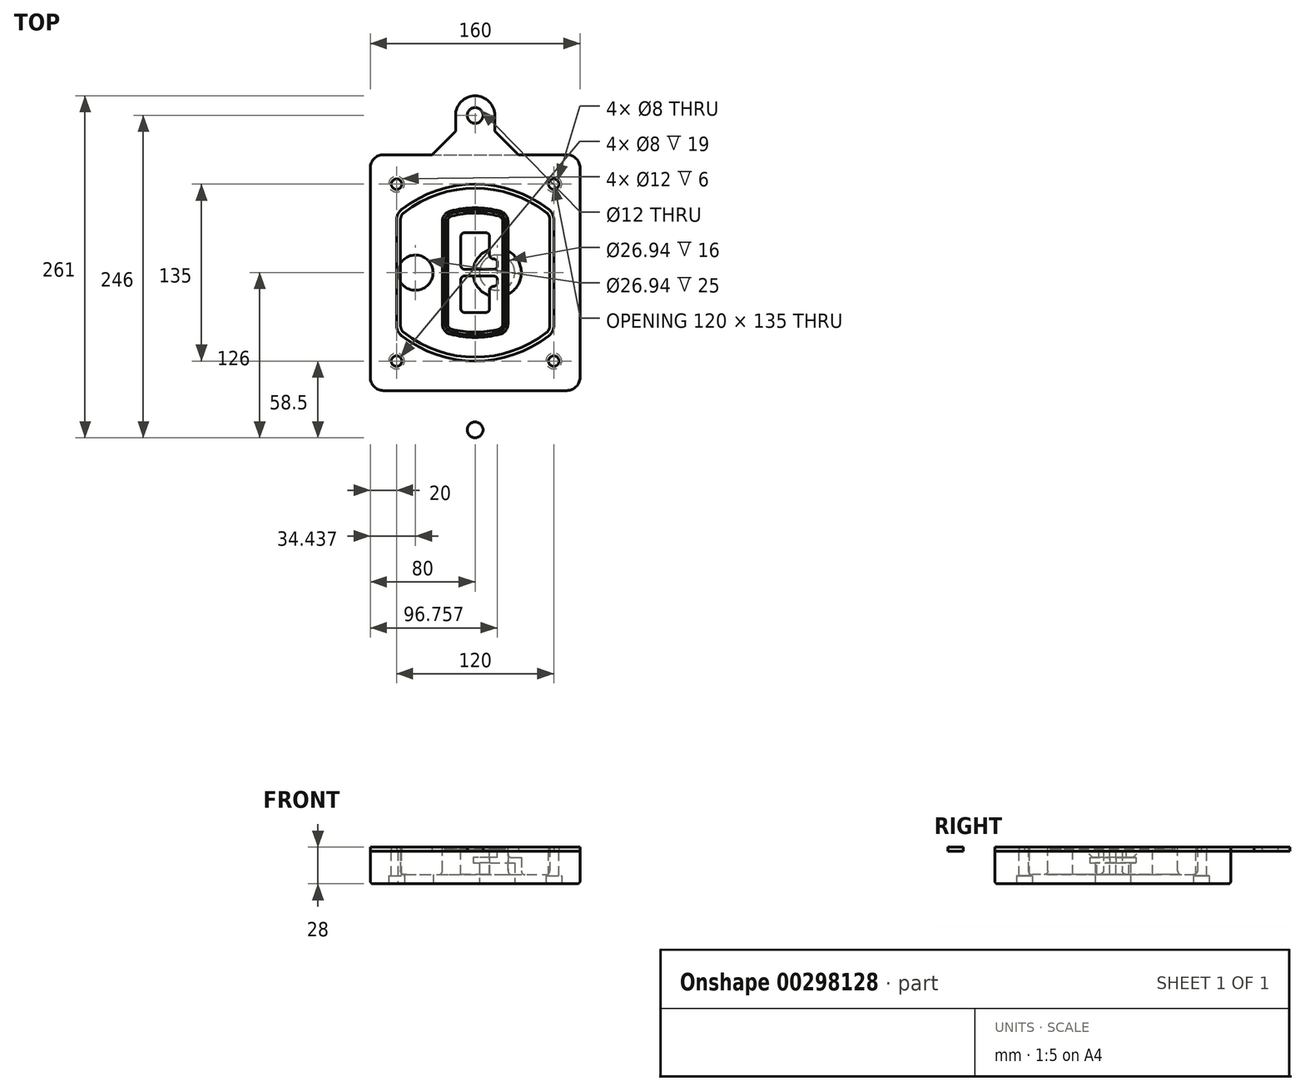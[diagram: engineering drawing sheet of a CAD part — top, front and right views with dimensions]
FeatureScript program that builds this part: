
annotation { "Feature Type Name" : "Feature", "Feature Type Description" : "" }
export const myFeature = defineFeature(function(context is Context, id is Id, definition is map)
    precondition{}
    {
        {
            var Q0;
            Q0=qCreatedBy(makeId("Top.planeOp"),FACE);
            var sketch = newSketch(context, id + "F0", { "sketchPlane" : qUnion([Q0])});
            skPoint(sketch, "E0.rect.middle", {"position": v(0, 0) * mm});
            skLineSegment(sketch, "E1.bottom", {"start": v(-70, -90) * mm, "end": v(70, -90) * mm});
            skLineSegment(sketch, "E1.top", {"start": v(-70, 90) * mm, "end": v(70, 90) * mm});
            skLineSegment(sketch, "E1.left", {"start": v(-80, -80) * mm, "end": v(-80, 80) * mm});
            skLineSegment(sketch, "E1.right", {"start": v(80, -80) * mm, "end": v(80, 80) * mm});
            skLineSegment(sketch, "E2", {"start": v(-80, 90) * mm, "end": v(80, -90) * mm, "construction": true});
            skLineSegment(sketch, "E3", {"start": v(80, 90) * mm, "end": v(-80, -90) * mm, "construction": true});
            skCircle(sketch, "E4", {"center": v(-60, 67.5) * mm, "radius": 4 * mm});
            skCircle(sketch, "E5", {"center": v(60, 67.5) * mm, "radius": 4 * mm});
            skCircle(sketch, "E6", {"center": v(60, -67.5) * mm, "radius": 4 * mm});
            skCircle(sketch, "E7", {"center": v(-60, -67.5) * mm, "radius": 4 * mm});
            skLineSegment(sketch, "E8", {"start": v(-60, 67.5) * mm, "end": v(60, 67.5) * mm, "construction": true});
            skLineSegment(sketch, "E9", {"start": v(60, 67.5) * mm, "end": v(60, -67.5) * mm, "construction": true});
            skLineSegment(sketch, "E10", {"start": v(60, -67.5) * mm, "end": v(-60, -67.5) * mm, "construction": true});
            skLineSegment(sketch, "E11", {"start": v(-60, -67.5) * mm, "end": v(-60, 67.5) * mm, "construction": true});
            skLineSegment(sketch, "E12", {"start": v(-60, 40.3) * mm, "end": v(-60, -40.3) * mm});
            skLineSegment(sketch, "E13", {"start": v(60, 40.3) * mm, "end": v(60, -40.3) * mm});
            skArc(sketch, "E14", {"start": v(56.15, 48.18) * mm, "mid": v(0, 67.5) * mm, "end": v(-56.15, 48.18) * mm});
            skArc(sketch, "E15", {"start": v(-56.15, -48.18) * mm, "mid": v(0, -67.5) * mm, "end": v(56.15, -48.18) * mm});
            skLineSegment(sketch, "E16", {"start": v(-60, 0) * mm, "end": v(60, 0) * mm, "construction": true});
            skPoint(sketch, "E17.visualSharp", {"position": v(-60, -45) * mm});
            skArc(sketch, "E17.filletArc", {"start": v(-60, -40.3) * mm, "mid": v(-58.99, -44.68) * mm, "end": v(-56.15, -48.18) * mm});
            skPoint(sketch, "E18.visualSharp", {"position": v(-60, 45) * mm});
            skArc(sketch, "E18.filletArc", {"start": v(-56.15, 48.18) * mm, "mid": v(-58.99, 44.68) * mm, "end": v(-60, 40.3) * mm});
            skPoint(sketch, "E19.visualSharp", {"position": v(60, 45) * mm});
            skArc(sketch, "E19.filletArc", {"start": v(60, 40.3) * mm, "mid": v(58.99, 44.68) * mm, "end": v(56.15, 48.18) * mm});
            skPoint(sketch, "E20.visualSharp", {"position": v(60, -45) * mm});
            skArc(sketch, "E20.filletArc", {"start": v(56.15, -48.18) * mm, "mid": v(58.99, -44.68) * mm, "end": v(60, -40.3) * mm});
            skPoint(sketch, "E21.visualSharp", {"position": v(-80, 90) * mm});
            skArc(sketch, "E21.filletArc", {"start": v(-70, 90) * mm, "mid": v(-77.07, 87.07) * mm, "end": v(-80, 80) * mm});
            skPoint(sketch, "E22.visualSharp", {"position": v(80, 90) * mm});
            skArc(sketch, "E22.filletArc", {"start": v(80, 80) * mm, "mid": v(77.07, 87.07) * mm, "end": v(70, 90) * mm});
            skPoint(sketch, "E23.visualSharp", {"position": v(80, -90) * mm});
            skArc(sketch, "E23.filletArc", {"start": v(70, -90) * mm, "mid": v(77.07, -87.07) * mm, "end": v(80, -80) * mm});
            skPoint(sketch, "E24.visualSharp", {"position": v(-80, -90) * mm});
            skArc(sketch, "E24.filletArc", {"start": v(-80, -80) * mm, "mid": v(-77.07, -87.07) * mm, "end": v(-70, -90) * mm});
            skArc(sketch, "E25.0", {"start": v(57, 40.3) * mm, "mid": v(56.3, 43.36) * mm, "end": v(54.3, 45.81) * mm});
            skLineSegment(sketch, "E25.1", {"start": v(57, 40.3) * mm, "end": v(57, -40.3) * mm});
            skArc(sketch, "E25.2", {"start": v(54.3, -45.81) * mm, "mid": v(56.3, -43.36) * mm, "end": v(57, -40.3) * mm});
            skArc(sketch, "E25.3", {"start": v(-54.3, -45.81) * mm, "mid": v(0, -64.5) * mm, "end": v(54.3, -45.81) * mm});
            skArc(sketch, "E25.4", {"start": v(-57, -40.3) * mm, "mid": v(-56.3, -43.36) * mm, "end": v(-54.3, -45.81) * mm});
            skArc(sketch, "E25.5", {"start": v(54.3, 45.81) * mm, "mid": v(0, 64.5) * mm, "end": v(-54.3, 45.81) * mm});
            skLineSegment(sketch, "E25.6", {"start": v(-57, 40.3) * mm, "end": v(-57, -40.3) * mm});
            skArc(sketch, "E25.7", {"start": v(-54.3, 45.81) * mm, "mid": v(-56.3, 43.36) * mm, "end": v(-57, 40.3) * mm});
            skArc(sketch, "E26.0", {"start": v(-58.62, 51.33) * mm, "mid": v(-62.58, 46.43) * mm, "end": v(-64, 40.3) * mm});
            skArc(sketch, "E26.1", {"start": v(58.62, 51.33) * mm, "mid": v(0, 71.5) * mm, "end": v(-58.62, 51.33) * mm});
            skArc(sketch, "E26.2", {"start": v(64, 40.3) * mm, "mid": v(62.58, 46.43) * mm, "end": v(58.62, 51.33) * mm});
            skLineSegment(sketch, "E26.3", {"start": v(64, 40.3) * mm, "end": v(64, -40.3) * mm});
            skArc(sketch, "E26.4", {"start": v(58.62, -51.33) * mm, "mid": v(62.58, -46.43) * mm, "end": v(64, -40.3) * mm});
            skLineSegment(sketch, "E26.5", {"start": v(-64, 40.3) * mm, "end": v(-64, -40.3) * mm});
            skArc(sketch, "E26.6", {"start": v(-58.62, -51.33) * mm, "mid": v(0, -71.5) * mm, "end": v(58.62, -51.33) * mm});
            skArc(sketch, "E26.7", {"start": v(-64, -40.3) * mm, "mid": v(-62.58, -46.43) * mm, "end": v(-58.62, -51.33) * mm});
            skSolve(sketch);
        }
        {
            var Q0;
            Q0=makeQuery(id+"F0.imprint","IMPRINT",FACE,{"disambiguationData":[TD([[makeQuery(id+"F0.imprint","IMPRINT",EDGE,{"derivedFrom":sQuery(id+"F0.wireOp",EDGE,"E1.bottom")}),1.0]])]});
            var Q1;
            Q1=makeQuery(id+"F0.imprint","IMPRINT",FACE,{"disambiguationData":[TD([[makeQuery(id+"F0.imprint","IMPRINT",EDGE,{"derivedFrom":sQuery(id+"F0.wireOp",EDGE,"E12")}),1.0]])]});
            var Q2;
            Q2=makeQuery(id+"F0.imprint","IMPRINT",FACE,{"disambiguationData":[TD([[makeQuery(id+"F0.imprint","IMPRINT",EDGE,{"derivedFrom":sQuery(id+"F0.wireOp",EDGE,"E25.0")}),1.0]])]});
            var Q3;
            Q3=makeQuery(id+"F0.imprint","IMPRINT",FACE,{"disambiguationData":[TD([[makeQuery(id+"F0.imprint","IMPRINT",EDGE,{"derivedFrom":sQuery(id+"F0.wireOp",EDGE,"E12")}),-1.0]])]});
            extrude(context, id + "F1", {"entities" : qUnion([Q0, Q1, Q2, Q3]), "oppositeDirection" : true, "depth" : 25 * mm});
        }
        {
            var Q0;
            Q0=makeQuery(id+"F0.imprint","IMPRINT",FACE,{"disambiguationData":[TD([[makeQuery(id+"F0.imprint","IMPRINT",EDGE,{"derivedFrom":sQuery(id+"F0.wireOp",EDGE,"E12")}),1.0]])]});
            extrude(context, id + "F2", {"entities" : qUnion([Q0]), "operationType" : NewBodyOperationType.ADD, "depth" : 3 * mm});
        }
        {
            var Q0;
            Q0=makeQuery(id+"F0.imprint","IMPRINT",FACE,{"disambiguationData":[TD([[makeQuery(id+"F0.imprint","IMPRINT",EDGE,{"derivedFrom":sQuery(id+"F0.wireOp",EDGE,"E25.0")}),1.0]])]});
            extrude(context, id + "F3", {"entities" : qUnion([Q0]), "operationType" : NewBodyOperationType.REMOVE, "oppositeDirection" : true, "depth" : 18 * mm});
        }
        {
            var Q0;
            Q0=makeQuery(id+"F2.opExtrude","CAP_FACE",FACE,{"disambiguationData":[OSD([sQuery(id+"F0.wireOp",EDGE,"E12"),sQuery(id+"F0.wireOp",EDGE,"E13"),sQuery(id+"F0.wireOp",EDGE,"E14"),sQuery(id+"F0.wireOp",EDGE,"E15"),sQuery(id+"F0.wireOp",EDGE,"E17.filletArc"),sQuery(id+"F0.wireOp",EDGE,"E18.filletArc"),sQuery(id+"F0.wireOp",EDGE,"E19.filletArc"),sQuery(id+"F0.wireOp",EDGE,"E20.filletArc"),sQuery(id+"F0.wireOp",EDGE,"E25.0"),sQuery(id+"F0.wireOp",EDGE,"E25.1"),sQuery(id+"F0.wireOp",EDGE,"E25.2"),sQuery(id+"F0.wireOp",EDGE,"E25.3"),sQuery(id+"F0.wireOp",EDGE,"E25.4"),sQuery(id+"F0.wireOp",EDGE,"E25.5"),sQuery(id+"F0.wireOp",EDGE,"E25.6"),sQuery(id+"F0.wireOp",EDGE,"E25.7")])],"isStart":false});
            var sketch = newSketch(context, id + "F4", { "sketchPlane" : qUnion([Q0])});
            skArc(sketch, "E27.0", {"start": v(-19.08, -46.97) * mm, "mid": v(0, -49.5) * mm, "end": v(19.08, -46.97) * mm});
            skArc(sketch, "E28.0", {"start": v(19.08, 46.97) * mm, "mid": v(0, 49.5) * mm, "end": v(-19.08, 46.97) * mm});
            skLineSegment(sketch, "E29", {"start": v(-25, 39.25) * mm, "end": v(-25, -39.25) * mm});
            skLineSegment(sketch, "E30", {"start": v(25, 39.25) * mm, "end": v(25, -39.25) * mm});
            skLineSegment(sketch, "E31", {"start": v(-25, 45.1) * mm, "end": v(25, 45.1) * mm, "construction": true});
            skLineSegment(sketch, "E32", {"start": v(-25, -45.1) * mm, "end": v(25, -45.1) * mm, "construction": true});
            skPoint(sketch, "E33.visualSharp", {"position": v(-25, 45.1) * mm});
            skArc(sketch, "E33.filletArc", {"start": v(-19.08, 46.97) * mm, "mid": v(-23.35, 44.11) * mm, "end": v(-25, 39.25) * mm});
            skPoint(sketch, "E34.visualSharp", {"position": v(25, 45.1) * mm});
            skArc(sketch, "E34.filletArc", {"start": v(25, 39.25) * mm, "mid": v(23.35, 44.11) * mm, "end": v(19.08, 46.97) * mm});
            skPoint(sketch, "E35.visualSharp", {"position": v(25, -45.1) * mm});
            skArc(sketch, "E35.filletArc", {"start": v(19.08, -46.97) * mm, "mid": v(23.35, -44.11) * mm, "end": v(25, -39.25) * mm});
            skPoint(sketch, "E36.visualSharp", {"position": v(-25, -45.1) * mm});
            skArc(sketch, "E36.filletArc", {"start": v(-25, -39.25) * mm, "mid": v(-23.35, -44.11) * mm, "end": v(-19.08, -46.97) * mm});
            skArc(sketch, "E37.0", {"start": v(54.3, 45.81) * mm, "mid": v(0, 64.5) * mm, "end": v(-54.3, 45.81) * mm});
            skArc(sketch, "E37.1", {"start": v(-54.3, 45.81) * mm, "mid": v(-56.3, 43.36) * mm, "end": v(-57, 40.3) * mm});
            skLineSegment(sketch, "E37.2", {"start": v(-57, 40.3) * mm, "end": v(-57, -40.3) * mm});
            skArc(sketch, "E37.3", {"start": v(-57, -40.3) * mm, "mid": v(-56.3, -43.36) * mm, "end": v(-54.3, -45.81) * mm});
            skArc(sketch, "E37.4", {"start": v(-54.3, -45.81) * mm, "mid": v(0, -64.5) * mm, "end": v(54.3, -45.81) * mm});
            skArc(sketch, "E37.5", {"start": v(54.3, -45.81) * mm, "mid": v(56.3, -43.36) * mm, "end": v(57, -40.3) * mm});
            skLineSegment(sketch, "E37.6", {"start": v(57, 40.3) * mm, "end": v(57, -40.3) * mm});
            skArc(sketch, "E37.7", {"start": v(57, 40.3) * mm, "mid": v(56.3, 43.36) * mm, "end": v(54.3, 45.81) * mm});
            skLineSegment(sketch, "E38.0", {"start": v(23, 39.25) * mm, "end": v(23, -39.25) * mm});
            skArc(sketch, "E38.1", {"start": v(18.56, -45.04) * mm, "mid": v(21.76, -42.9) * mm, "end": v(23, -39.25) * mm});
            skArc(sketch, "E38.2", {"start": v(-18.56, -45.04) * mm, "mid": v(0, -47.5) * mm, "end": v(18.56, -45.04) * mm});
            skArc(sketch, "E38.3", {"start": v(-23, -39.25) * mm, "mid": v(-21.76, -42.9) * mm, "end": v(-18.56, -45.04) * mm});
            skLineSegment(sketch, "E38.4", {"start": v(-23, 39.25) * mm, "end": v(-23, -39.25) * mm});
            skArc(sketch, "E38.5", {"start": v(23, 39.25) * mm, "mid": v(21.76, 42.9) * mm, "end": v(18.56, 45.04) * mm});
            skArc(sketch, "E38.6", {"start": v(-18.56, 45.04) * mm, "mid": v(-21.76, 42.9) * mm, "end": v(-23, 39.25) * mm});
            skArc(sketch, "E38.7", {"start": v(18.56, 45.04) * mm, "mid": v(0, 47.5) * mm, "end": v(-18.56, 45.04) * mm});
            skArc(sketch, "E39.0", {"start": v(21, 39.25) * mm, "mid": v(20.18, 41.68) * mm, "end": v(18.04, 43.1) * mm});
            skLineSegment(sketch, "E39.1", {"start": v(21, 39.25) * mm, "end": v(21, -39.25) * mm});
            skArc(sketch, "E39.2", {"start": v(18.04, -43.1) * mm, "mid": v(20.18, -41.68) * mm, "end": v(21, -39.25) * mm});
            skArc(sketch, "E39.3", {"start": v(-18.04, -43.1) * mm, "mid": v(0, -45.5) * mm, "end": v(18.04, -43.1) * mm});
            skArc(sketch, "E39.4", {"start": v(-21, -39.25) * mm, "mid": v(-20.18, -41.68) * mm, "end": v(-18.04, -43.1) * mm});
            skArc(sketch, "E39.5", {"start": v(18.04, 43.1) * mm, "mid": v(0, 45.5) * mm, "end": v(-18.04, 43.1) * mm});
            skLineSegment(sketch, "E39.6", {"start": v(-21, 39.25) * mm, "end": v(-21, -39.25) * mm});
            skArc(sketch, "E39.7", {"start": v(-18.04, 43.1) * mm, "mid": v(-20.18, 41.68) * mm, "end": v(-21, 39.25) * mm});
            skLineSegment(sketch, "E40", {"start": v(-25, 0) * mm, "end": v(25, 0) * mm, "construction": true});
            skLineSegment(sketch, "E41", {"start": v(-11, 5.5) * mm, "end": v(-11, 27.5) * mm});
            skLineSegment(sketch, "E42", {"start": v(-8, 30.5) * mm, "end": v(8, 30.5) * mm});
            skLineSegment(sketch, "E43", {"start": v(11, 27.5) * mm, "end": v(11, 13.5) * mm});
            skLineSegment(sketch, "E44", {"start": v(14, 10.5) * mm, "end": v(14, 10.5) * mm});
            skLineSegment(sketch, "E45", {"start": v(17, 7.5) * mm, "end": v(17, 5.5) * mm});
            skLineSegment(sketch, "E46", {"start": v(14, 2.5) * mm, "end": v(-8, 2.5) * mm});
            skPoint(sketch, "E47.visualSharp", {"position": v(-11, 30.5) * mm});
            skArc(sketch, "E47.filletArc", {"start": v(-8, 30.5) * mm, "mid": v(-10.12, 29.62) * mm, "end": v(-11, 27.5) * mm});
            skPoint(sketch, "E48.visualSharp", {"position": v(11, 30.5) * mm});
            skArc(sketch, "E48.filletArc", {"start": v(11, 27.5) * mm, "mid": v(10.12, 29.62) * mm, "end": v(8, 30.5) * mm});
            skPoint(sketch, "E49.visualSharp", {"position": v(11, 10.5) * mm});
            skArc(sketch, "E49.filletArc", {"start": v(11, 13.5) * mm, "mid": v(11.88, 11.38) * mm, "end": v(14, 10.5) * mm});
            skPoint(sketch, "E50.visualSharp", {"position": v(17, 10.5) * mm});
            skArc(sketch, "E50.filletArc", {"start": v(17, 7.5) * mm, "mid": v(16.12, 9.62) * mm, "end": v(14, 10.5) * mm});
            skPoint(sketch, "E51.visualSharp", {"position": v(17, 2.5) * mm});
            skArc(sketch, "E51.filletArc", {"start": v(14, 2.5) * mm, "mid": v(16.12, 3.38) * mm, "end": v(17, 5.5) * mm});
            skPoint(sketch, "E52.visualSharp", {"position": v(-11, 2.5) * mm});
            skArc(sketch, "E52.filletArc", {"start": v(-11, 5.5) * mm, "mid": v(-10.12, 3.38) * mm, "end": v(-8, 2.5) * mm});
            skLineSegment(sketch, "E53.0.MirrorCS", {"start": v(14, -2.5) * mm, "end": v(-8, -2.5) * mm});
            skArc(sketch, "E54.0.MirrorCS", {"start": v(-11, -5.5) * mm, "mid": v(-10.12, -3.38) * mm, "end": v(-8, -2.5) * mm});
            skLineSegment(sketch, "E55.0.MirrorCS", {"start": v(-11, -5.5) * mm, "end": v(-11, -27.5) * mm});
            skArc(sketch, "E56.0.MirrorCS", {"start": v(-8, -30.5) * mm, "mid": v(-10.12, -29.62) * mm, "end": v(-11, -27.5) * mm});
            skLineSegment(sketch, "E57.0.MirrorCS", {"start": v(-8, -30.5) * mm, "end": v(8, -30.5) * mm});
            skArc(sketch, "E58.0.MirrorCS", {"start": v(11, -27.5) * mm, "mid": v(10.12, -29.62) * mm, "end": v(8, -30.5) * mm});
            skLineSegment(sketch, "E59.0.MirrorCS", {"start": v(11, -27.5) * mm, "end": v(11, -13.5) * mm});
            skArc(sketch, "E60.0.MirrorCS", {"start": v(11, -13.5) * mm, "mid": v(11.88, -11.38) * mm, "end": v(14, -10.5) * mm});
            skArc(sketch, "E61.0.MirrorCS", {"start": v(17, -7.5) * mm, "mid": v(16.12, -9.62) * mm, "end": v(14, -10.5) * mm});
            skLineSegment(sketch, "E62.0.MirrorCS", {"start": v(17, -7.5) * mm, "end": v(17, -5.5) * mm});
            skArc(sketch, "E63.0.MirrorCS", {"start": v(14, -2.5) * mm, "mid": v(16.12, -3.38) * mm, "end": v(17, -5.5) * mm});
            skSolve(sketch);
        }
        {
            var Q0;
            Q0=makeQuery(id+"F4.imprint","IMPRINT",FACE,{"disambiguationData":[TD([[makeQuery(id+"F4.imprint","IMPRINT",EDGE,{"derivedFrom":sQuery(id+"F4.wireOp",EDGE,"E27.0")}),1.0]])]});
            var Q1;
            Q1=makeQuery(id+"F4.imprint","IMPRINT",FACE,{"disambiguationData":[TD([[makeQuery(id+"F4.imprint","IMPRINT",EDGE,{"derivedFrom":sQuery(id+"F4.wireOp",EDGE,"E38.0")}),-1.0]])]});
            var Q2;
            Q2=makeQuery(id+"F4.imprint","IMPRINT",FACE,{"disambiguationData":[TD([[makeQuery(id+"F4.imprint","IMPRINT",EDGE,{"derivedFrom":sQuery(id+"F4.wireOp",EDGE,"E39.0")}),1.0]])]});
            extrude(context, id + "F5", {"entities" : qUnion([Q0, Q1, Q2]), "operationType" : NewBodyOperationType.ADD, "endBound" : BoundingType.UP_TO_NEXT, "oppositeDirection" : true, "depth" : 25 * mm});
        }
        {
            var Q0;
            Q0=makeQuery(id+"F4.imprint","IMPRINT",FACE,{"disambiguationData":[TD([[makeQuery(id+"F4.imprint","IMPRINT",EDGE,{"derivedFrom":sQuery(id+"F4.wireOp",EDGE,"E38.0")}),-1.0]])]});
            extrude(context, id + "F6", {"entities" : qUnion([Q0]), "operationType" : NewBodyOperationType.REMOVE, "oppositeDirection" : true, "depth" : 2 * mm});
        }
        {
            var Q0;
            Q0=makeQuery(id+"F1.opExtrude","CAP_FACE",FACE,{"disambiguationData":[OSD([sQuery(id+"F0.wireOp",EDGE,"E1.bottom"),sQuery(id+"F0.wireOp",EDGE,"E1.top"),sQuery(id+"F0.wireOp",EDGE,"E1.left"),sQuery(id+"F0.wireOp",EDGE,"E1.right"),sQuery(id+"F0.wireOp",EDGE,"E4"),sQuery(id+"F0.wireOp",EDGE,"E5"),sQuery(id+"F0.wireOp",EDGE,"E6"),sQuery(id+"F0.wireOp",EDGE,"E7"),sQuery(id+"F0.wireOp",EDGE,"E21.filletArc"),sQuery(id+"F0.wireOp",EDGE,"E22.filletArc"),sQuery(id+"F0.wireOp",EDGE,"E23.filletArc"),sQuery(id+"F0.wireOp",EDGE,"E24.filletArc")])],"isStart":false});
            var sketch = newSketch(context, id + "F7", { "sketchPlane" : qUnion([Q0])});
            skCircle(sketch, "E64", {"center": v(16.76, 0) * mm, "radius": 13.47 * mm});
            skCircle(sketch, "E65", {"center": v(-45.56, 0) * mm, "radius": 13.47 * mm});
            skLineSegment(sketch, "E66", {"start": v(80, 0) * mm, "end": v(-80, 0) * mm});
            skCircle(sketch, "E67", {"center": v(16.76, 0) * mm, "radius": 18.47 * mm});
            skCircle(sketch, "E68", {"center": v(60, -67.5) * mm, "radius": 6 * mm});
            skCircle(sketch, "E69", {"center": v(-60, -67.5) * mm, "radius": 6 * mm});
            skCircle(sketch, "E70", {"center": v(-60, 67.5) * mm, "radius": 6 * mm});
            skCircle(sketch, "E71", {"center": v(60, 67.5) * mm, "radius": 6 * mm});
            skSolve(sketch);
        }
        {
            var Q0;
            {var subQ1=sQuery(id+"F7.wireOp",EDGE,"E66");var subQ4=sQuery(id+"F7.wireOp",EDGE,"E64");var subQ6=makeQuery(id+"F7.imprint","INTERSECT",VERTEX,{"disambiguationData":[OD(0.0)],"derivedFrom":[subQ4,subQ1]});Q0=makeQuery(id+"F7.imprint","IMPRINT",FACE,{"disambiguationData":[TD([[makeQuery(id+"F7.imprint","IMPRINT",EDGE,{"disambiguationData":[TD([[subQ6,-1.0]])],"derivedFrom":subQ4}),-1.0]])]});}
            var Q1;
            {var subQ0=sQuery(id+"F7.wireOp",EDGE,"E66");var subQ1=sQuery(id+"F7.wireOp",EDGE,"E64");var subQ3=makeQuery(id+"F7.imprint","INTERSECT",VERTEX,{"disambiguationData":[OD(0.0)],"derivedFrom":[subQ1,subQ0]});Q1=makeQuery(id+"F7.imprint","IMPRINT",FACE,{"disambiguationData":[TD([[makeQuery(id+"F7.imprint","IMPRINT",EDGE,{"disambiguationData":[TD([[subQ3,-1.0]])],"derivedFrom":subQ1}),1.0]])]});}
            var Q2;
            {var subQ0=sQuery(id+"F7.wireOp",EDGE,"E66");var subQ1=sQuery(id+"F7.wireOp",EDGE,"E64");var subQ3=makeQuery(id+"F7.imprint","INTERSECT",VERTEX,{"disambiguationData":[OD(0.0)],"derivedFrom":[subQ1,subQ0]});Q2=makeQuery(id+"F7.imprint","IMPRINT",FACE,{"disambiguationData":[TD([[makeQuery(id+"F7.imprint","IMPRINT",EDGE,{"disambiguationData":[TD([[subQ3,1.0]])],"derivedFrom":subQ1}),1.0]])]});}
            var Q3;
            {var subQ1=sQuery(id+"F7.wireOp",EDGE,"E66");var subQ4=sQuery(id+"F7.wireOp",EDGE,"E64");var subQ6=makeQuery(id+"F7.imprint","INTERSECT",VERTEX,{"disambiguationData":[OD(0.0)],"derivedFrom":[subQ4,subQ1]});Q3=makeQuery(id+"F7.imprint","IMPRINT",FACE,{"disambiguationData":[TD([[makeQuery(id+"F7.imprint","IMPRINT",EDGE,{"disambiguationData":[TD([[subQ6,1.0]])],"derivedFrom":subQ4}),-1.0]])]});}
            extrude(context, id + "F8", {"entities" : qUnion([Q0, Q1, Q2, Q3]), "operationType" : NewBodyOperationType.ADD, "oppositeDirection" : true, "depth" : 20 * mm});
        }
        {
            var Q0;
            {var subQ0=sQuery(id+"F7.wireOp",EDGE,"E66");var subQ1=sQuery(id+"F7.wireOp",EDGE,"E64");var subQ3=makeQuery(id+"F7.imprint","INTERSECT",VERTEX,{"disambiguationData":[OD(0.0)],"derivedFrom":[subQ1,subQ0]});Q0=makeQuery(id+"F7.imprint","IMPRINT",FACE,{"disambiguationData":[TD([[makeQuery(id+"F7.imprint","IMPRINT",EDGE,{"disambiguationData":[TD([[subQ3,-1.0]])],"derivedFrom":subQ1}),1.0]])]});}
            var Q1;
            {var subQ0=sQuery(id+"F7.wireOp",EDGE,"E66");var subQ1=sQuery(id+"F7.wireOp",EDGE,"E64");var subQ3=makeQuery(id+"F7.imprint","INTERSECT",VERTEX,{"disambiguationData":[OD(0.0)],"derivedFrom":[subQ1,subQ0]});Q1=makeQuery(id+"F7.imprint","IMPRINT",FACE,{"disambiguationData":[TD([[makeQuery(id+"F7.imprint","IMPRINT",EDGE,{"disambiguationData":[TD([[subQ3,1.0]])],"derivedFrom":subQ1}),1.0]])]});}
            extrude(context, id + "F9", {"entities" : qUnion([Q0, Q1]), "operationType" : NewBodyOperationType.REMOVE, "oppositeDirection" : true, "depth" : 16 * mm});
        }
        {
            var Q0;
            {var subQ0=sQuery(id+"F7.wireOp",EDGE,"E66");var subQ1=sQuery(id+"F7.wireOp",EDGE,"E65");var subQ3=makeQuery(id+"F7.imprint","INTERSECT",VERTEX,{"disambiguationData":[OD(0.0)],"derivedFrom":[subQ1,subQ0]});Q0=makeQuery(id+"F7.imprint","IMPRINT",FACE,{"disambiguationData":[TD([[makeQuery(id+"F7.imprint","IMPRINT",EDGE,{"disambiguationData":[TD([[subQ3,-1.0]])],"derivedFrom":subQ1}),1.0]])]});}
            var Q1;
            {var subQ0=sQuery(id+"F7.wireOp",EDGE,"E66");var subQ1=sQuery(id+"F7.wireOp",EDGE,"E65");var subQ3=makeQuery(id+"F7.imprint","INTERSECT",VERTEX,{"disambiguationData":[OD(0.0)],"derivedFrom":[subQ1,subQ0]});Q1=makeQuery(id+"F7.imprint","IMPRINT",FACE,{"disambiguationData":[TD([[makeQuery(id+"F7.imprint","IMPRINT",EDGE,{"disambiguationData":[TD([[subQ3,1.0]])],"derivedFrom":subQ1}),1.0]])]});}
            extrude(context, id + "F10", {"entities" : qUnion([Q0, Q1]), "operationType" : NewBodyOperationType.REMOVE, "oppositeDirection" : true, "depth" : 25 * mm});
        }
        {
            var Q0;
            Q0=makeQuery(id+"F7.imprint","IMPRINT",FACE,{"disambiguationData":[TD([[makeQuery(id+"F7.imprint","IMPRINT",EDGE,{"derivedFrom":sQuery(id+"F7.wireOp",EDGE,"E68")}),1.0]])]});
            var Q1;
            Q1=makeQuery(id+"F7.imprint","IMPRINT",FACE,{"disambiguationData":[TD([[makeQuery(id+"F7.imprint","IMPRINT",EDGE,{"derivedFrom":makeQuery(id+"F1.opExtrude","CAP_EDGE",EDGE,{"disambiguationData":[OSD([sQuery(id+"F0.wireOp",EDGE,"E5")])],"isStart":false})}),-1.0]])]});
            var Q2;
            Q2=makeQuery(id+"F7.imprint","IMPRINT",FACE,{"disambiguationData":[TD([[makeQuery(id+"F7.imprint","IMPRINT",EDGE,{"derivedFrom":sQuery(id+"F7.wireOp",EDGE,"E69")}),1.0]])]});
            var Q3;
            Q3=makeQuery(id+"F7.imprint","IMPRINT",FACE,{"disambiguationData":[TD([[makeQuery(id+"F7.imprint","IMPRINT",EDGE,{"derivedFrom":makeQuery(id+"F1.opExtrude","CAP_EDGE",EDGE,{"disambiguationData":[OSD([sQuery(id+"F0.wireOp",EDGE,"E4")])],"isStart":false})}),-1.0]])]});
            var Q4;
            Q4=makeQuery(id+"F7.imprint","IMPRINT",FACE,{"disambiguationData":[TD([[makeQuery(id+"F7.imprint","IMPRINT",EDGE,{"derivedFrom":sQuery(id+"F7.wireOp",EDGE,"E70")}),1.0]])]});
            var Q5;
            Q5=makeQuery(id+"F7.imprint","IMPRINT",FACE,{"disambiguationData":[TD([[makeQuery(id+"F7.imprint","IMPRINT",EDGE,{"derivedFrom":makeQuery(id+"F1.opExtrude","CAP_EDGE",EDGE,{"disambiguationData":[OSD([sQuery(id+"F0.wireOp",EDGE,"E7")])],"isStart":false})}),-1.0]])]});
            var Q6;
            Q6=makeQuery(id+"F7.imprint","IMPRINT",FACE,{"disambiguationData":[TD([[makeQuery(id+"F7.imprint","IMPRINT",EDGE,{"derivedFrom":sQuery(id+"F7.wireOp",EDGE,"E71")}),1.0]])]});
            var Q7;
            Q7=makeQuery(id+"F7.imprint","IMPRINT",FACE,{"disambiguationData":[TD([[makeQuery(id+"F7.imprint","IMPRINT",EDGE,{"derivedFrom":makeQuery(id+"F1.opExtrude","CAP_EDGE",EDGE,{"disambiguationData":[OSD([sQuery(id+"F0.wireOp",EDGE,"E6")])],"isStart":false})}),-1.0]])]});
            extrude(context, id + "F11", {"entities" : qUnion([Q0, Q1, Q2, Q3, Q4, Q5, Q6, Q7]), "operationType" : NewBodyOperationType.REMOVE, "oppositeDirection" : true, "depth" : 6 * mm});
        }
        {
            var Q0;
            Q0=makeQuery(id+"F9.boolean.opBoolean","COPY",FACE,{"derivedFrom":makeQuery(id+"F9.opExtrude","CAP_FACE",FACE,{"disambiguationData":[OSD([sQuery(id+"F7.wireOp",EDGE,"E64")])],"isStart":false})});
            var sketch = newSketch(context, id + "F12", { "sketchPlane" : qUnion([Q0])});
            skArc(sketch, "E72.0", {"start": v(11, 17.55) * mm, "mid": v(2.57, 11.82) * mm, "end": v(-1.54, 2.5) * mm});
            skArc(sketch, "E72.1", {"start": v(-1.54, -2.5) * mm, "mid": v(2.57, -11.82) * mm, "end": v(11, -17.55) * mm});
            skLineSegment(sketch, "E73", {"start": v(-1.54, -2.5) * mm, "end": v(14, -2.5) * mm});
            skLineSegment(sketch, "E74.0", {"start": v(14, 2.5) * mm, "end": v(-1.54, 2.5) * mm});
            skArc(sketch, "E74.1", {"start": v(14, 2.5) * mm, "mid": v(16.12, 3.38) * mm, "end": v(17, 5.5) * mm});
            skLineSegment(sketch, "E74.2", {"start": v(17, 7.5) * mm, "end": v(17, 5.5) * mm});
            skArc(sketch, "E74.3", {"start": v(17, 7.5) * mm, "mid": v(16.12, 9.62) * mm, "end": v(14, 10.5) * mm});
            skArc(sketch, "E74.4", {"start": v(11, 13.5) * mm, "mid": v(11.88, 11.38) * mm, "end": v(14, 10.5) * mm});
            skLineSegment(sketch, "E74.5", {"start": v(11, 17.55) * mm, "end": v(11, 13.5) * mm});
            skLineSegment(sketch, "E74.7", {"start": v(14, -2.5) * mm, "end": v(-1.54, -2.5) * mm});
            skArc(sketch, "E74.8", {"start": v(14, -2.5) * mm, "mid": v(16.12, -3.38) * mm, "end": v(17, -5.5) * mm});
            skLineSegment(sketch, "E74.9", {"start": v(17, -7.5) * mm, "end": v(17, -5.5) * mm});
            skArc(sketch, "E74.10", {"start": v(17, -7.5) * mm, "mid": v(16.12, -9.62) * mm, "end": v(14, -10.5) * mm});
            skArc(sketch, "E74.11", {"start": v(11, -13.5) * mm, "mid": v(11.88, -11.38) * mm, "end": v(14, -10.5) * mm});
            skLineSegment(sketch, "E74.12", {"start": v(11, -17.55) * mm, "end": v(11, -13.5) * mm});
            skPoint(sketch, "E75.orphan", {"position": v(11, -27.5) * mm});
            skPoint(sketch, "E76.orphan", {"position": v(-8, -2.5) * mm});
            skPoint(sketch, "E77.orphan", {"position": v(-8, 2.5) * mm});
            skPoint(sketch, "E78.orphan", {"position": v(11, 27.5) * mm});
            skSolve(sketch);
        }
        {
            var Q0;
            {var subQ7=sQuery(id+"F12.wireOp",EDGE,"E72.0");var subQ14=sQuery(id+"F12.wireOp",EDGE,"E72.1");var subQ16=sQuery(id+"F12.wireOp",EDGE,"E74.1");var subQ18=sQuery(id+"F12.wireOp",EDGE,"E74.8");Q0=qUnion([makeQuery(id+"F12.imprint","IMPRINT",FACE,{"disambiguationData":[TD([[makeQuery(id+"F12.imprint","IMPRINT",EDGE,{"derivedFrom":subQ7}),1.0]])]}),makeQuery(id+"F12.imprint","IMPRINT",FACE,{"disambiguationData":[TD([[makeQuery(id+"F12.imprint","IMPRINT",EDGE,{"derivedFrom":subQ14}),1.0]])]}),makeQuery(id+"F12.imprint","IMPRINT",FACE,{"disambiguationData":[TD([[makeQuery(id+"F12.imprint","IMPRINT",EDGE,{"derivedFrom":subQ16}),1.0]])]}),makeQuery(id+"F12.imprint","IMPRINT",FACE,{"disambiguationData":[TD([[makeQuery(id+"F12.imprint","IMPRINT",EDGE,{"derivedFrom":subQ18}),-1.0]])]})]);}
            var Q1;
            Q1=makeQuery(id+"F5.boolean.opBoolean","SPLIT",FACE,{"disambiguationData":[TD([makeQuery(id+"F5.opExtrude","SWEPT_FACE",FACE,{"disambiguationData":[OSD([sQuery(id+"F4.wireOp",EDGE,"E41")])]})])],"derivedFrom":makeQuery(id+"F3.boolean.opBoolean","COPY",FACE,{"derivedFrom":makeQuery(id+"F3.opExtrude","CAP_FACE",FACE,{"disambiguationData":[OSD([sQuery(id+"F0.wireOp",EDGE,"E25.0"),sQuery(id+"F0.wireOp",EDGE,"E25.1"),sQuery(id+"F0.wireOp",EDGE,"E25.2"),sQuery(id+"F0.wireOp",EDGE,"E25.3"),sQuery(id+"F0.wireOp",EDGE,"E25.4"),sQuery(id+"F0.wireOp",EDGE,"E25.5"),sQuery(id+"F0.wireOp",EDGE,"E25.6"),sQuery(id+"F0.wireOp",EDGE,"E25.7")])],"isStart":false})})});
            extrude(context, id + "F13", {"entities" : qUnion([Q0]), "operationType" : NewBodyOperationType.REMOVE, "endBound" : BoundingType.UP_TO_SURFACE, "endBoundEntityFace" : qUnion([Q1]), "depth" : 25 * mm});
        }
        {
            var Q0;
            Q0=makeQuery(id+"F3.boolean.opBoolean","COPY",EDGE,{"derivedFrom":makeQuery(id+"F3.opExtrude","CAP_EDGE",EDGE,{"disambiguationData":[OSD([sQuery(id+"F0.wireOp",EDGE,"E25.6")])],"isStart":false})});
            var Q1;
            Q1=makeQuery(id+"F8.boolean.opBoolean","INTERSECT",EDGE,{"derivedFrom":[makeQuery(id+"F5.opExtrude","SWEPT_FACE",FACE,{"disambiguationData":[OSD([sQuery(id+"F4.wireOp",EDGE,"E30")])]}),makeQuery(id+"F8.opExtrude","CAP_FACE",FACE,{"disambiguationData":[OSD([sQuery(id+"F7.wireOp",EDGE,"E67")])],"isStart":false})]});
            var Q2;
            Q2=makeQuery(id+"F8.boolean.opBoolean","INTERSECT",EDGE,{"disambiguationData":[OD(1.0)],"derivedFrom":[makeQuery(id+"F5.opExtrude","SWEPT_FACE",FACE,{"disambiguationData":[OSD([sQuery(id+"F4.wireOp",EDGE,"E30")])]}),makeQuery(id+"F8.opExtrude","SWEPT_FACE",FACE,{"disambiguationData":[OSD([sQuery(id+"F7.wireOp",EDGE,"E67")])]})]});
            var Q3;
            {var subQ0=sQuery(id+"F4.wireOp",EDGE,"E30");Q3=makeQuery(id+"F8.boolean.opBoolean","SPLIT",EDGE,{"disambiguationData":[TD([makeQuery(id+"F5.opExtrude","SWEPT_FACE",FACE,{"disambiguationData":[OSD([sQuery(id+"F4.wireOp",EDGE,"E35.filletArc")])]})])],"derivedFrom":makeQuery(id+"F5.opExtrude","CAP_EDGE",EDGE,{"disambiguationData":[OSD([subQ0])],"isStart":false})});}
            var Q4;
            {var subQ0=sQuery(id+"F0.wireOp",EDGE,"E25.7");var subQ1=sQuery(id+"F0.wireOp",EDGE,"E25.1");var subQ2=sQuery(id+"F0.wireOp",EDGE,"E25.6");var subQ3=sQuery(id+"F0.wireOp",EDGE,"E25.5");var subQ4=sQuery(id+"F0.wireOp",EDGE,"E25.4");var subQ5=sQuery(id+"F0.wireOp",EDGE,"E25.0");var subQ6=sQuery(id+"F0.wireOp",EDGE,"E25.2");var subQ7=sQuery(id+"F0.wireOp",EDGE,"E25.3");Q4=makeQuery(id+"F8.boolean.opBoolean","INTERSECT",EDGE,{"derivedFrom":[makeQuery(id+"F5.boolean.opBoolean","SPLIT",FACE,{"disambiguationData":[TD([makeQuery(id+"F2.opExtrude","SWEPT_FACE",FACE,{"disambiguationData":[OSD([subQ5])]})])],"derivedFrom":makeQuery(id+"F3.boolean.opBoolean","COPY",FACE,{"derivedFrom":makeQuery(id+"F3.opExtrude","CAP_FACE",FACE,{"disambiguationData":[OSD([subQ5,subQ1,subQ6,subQ7,subQ4,subQ3,subQ2,subQ0])],"isStart":false})})}),makeQuery(id+"F8.opExtrude","SWEPT_FACE",FACE,{"disambiguationData":[OSD([sQuery(id+"F7.wireOp",EDGE,"E67")])]})]});}
            var Q5;
            Q5=makeQuery(id+"F8.boolean.opBoolean","INTERSECT",EDGE,{"disambiguationData":[OD(0.0)],"derivedFrom":[makeQuery(id+"F5.opExtrude","SWEPT_FACE",FACE,{"disambiguationData":[OSD([sQuery(id+"F4.wireOp",EDGE,"E30")])]}),makeQuery(id+"F8.opExtrude","SWEPT_FACE",FACE,{"disambiguationData":[OSD([sQuery(id+"F7.wireOp",EDGE,"E67")])]})]});
            fillet(context, id + "F14", {"entities" : qUnion([Q0, Q1, Q2, Q3, Q4, Q5]), "radius" : 3 * mm, "tangentPropagation" : true, "allowEdgeOverflow" : false});
        }
        {
            var Q0;
            Q0=makeQuery(id+"F1.opExtrude","CAP_EDGE",EDGE,{"disambiguationData":[OSD([sQuery(id+"F0.wireOp",EDGE,"E1.bottom")])],"isStart":false});
            fillet(context, id + "F15", {"entities" : qUnion([Q0]), "radius" : 2 * mm, "tangentPropagation" : true, "allowEdgeOverflow" : false});
        }
        {
            var Q0;
            {var subQ0=sQuery(id+"F0.wireOp",EDGE,"E21.filletArc");var subQ1=sQuery(id+"F0.wireOp",EDGE,"E7");var subQ2=sQuery(id+"F0.wireOp",EDGE,"E6");var subQ3=sQuery(id+"F0.wireOp",EDGE,"E5");var subQ4=sQuery(id+"F0.wireOp",EDGE,"E4");var subQ5=sQuery(id+"F0.wireOp",EDGE,"E22.filletArc");var subQ6=sQuery(id+"F0.wireOp",EDGE,"E1.bottom");var subQ7=sQuery(id+"F0.wireOp",EDGE,"E1.right");var subQ8=sQuery(id+"F0.wireOp",EDGE,"E1.top");var subQ9=sQuery(id+"F0.wireOp",EDGE,"E1.left");var subQ10=sQuery(id+"F0.wireOp",EDGE,"E23.filletArc");var subQ11=sQuery(id+"F0.wireOp",EDGE,"E24.filletArc");Q0=makeQuery(id+"F2.boolean.opBoolean","SPLIT",FACE,{"disambiguationData":[TD([makeQuery(id+"F1.opExtrude","SWEPT_FACE",FACE,{"disambiguationData":[OSD([subQ6])]})])],"derivedFrom":makeQuery(id+"F1.opExtrude","CAP_FACE",FACE,{"disambiguationData":[OSD([subQ6,subQ8,subQ9,subQ7,subQ4,subQ3,subQ2,subQ1,subQ0,subQ5,subQ10,subQ11])],"isStart":true})});}
            var sketch = newSketch(context, id + "F16", { "sketchPlane" : qUnion([Q0])});
            skLineSegment(sketch, "E79", {"start": v(0, 90) * mm, "end": v(0, 120) * mm, "construction": true});
            skCircle(sketch, "E80", {"center": v(0, 120) * mm, "radius": 6 * mm});
            skArc(sketch, "E81", {"start": v(15, 120) * mm, "mid": v(0, 135) * mm, "end": v(-15, 120) * mm});
            skLineSegment(sketch, "E82", {"start": v(-15, 120) * mm, "end": v(-15, 108) * mm});
            skLineSegment(sketch, "E83", {"start": v(-15, 108) * mm, "end": v(-33, 90) * mm});
            skLineSegment(sketch, "E84", {"start": v(15, 120) * mm, "end": v(15, 108) * mm});
            skLineSegment(sketch, "E85", {"start": v(15, 108) * mm, "end": v(33, 90) * mm});
            skLineSegment(sketch, "E86", {"start": v(-80, 0) * mm, "end": v(80, 0) * mm, "construction": true});
            skCircle(sketch, "E87.MirrorC", {"center": v(0, -120) * mm, "radius": 6 * mm});
            skLineSegment(sketch, "E88.MirrorCS", {"start": v(-15, -120) * mm, "end": v(-15, -108) * mm});
            skArc(sketch, "E89.MirrorCS", {"start": v(15, -120) * mm, "mid": v(0, -135) * mm, "end": v(-15, -120) * mm});
            skLineSegment(sketch, "E90.MirrorCS", {"start": v(15, -120) * mm, "end": v(15, -108) * mm});
            skLineSegment(sketch, "E91.MirrorCS", {"start": v(15, -108) * mm, "end": v(33, -90) * mm});
            skLineSegment(sketch, "E92.MirrorCS", {"start": v(-15, -108) * mm, "end": v(-33, -90) * mm});
            skSolve(sketch);
        }
        {
            var Q0;
            Q0=makeQuery(id+"F16.imprint","IMPRINT",FACE,{"disambiguationData":[TD([[makeQuery(id+"F16.imprint","IMPRINT",EDGE,{"derivedFrom":makeQuery(id+"F1.opExtrude","CAP_EDGE",EDGE,{"disambiguationData":[OSD([sQuery(id+"F0.wireOp",EDGE,"E1.left")])],"isStart":true})}),-1.0]])]});
            var Q1;
            Q1=makeQuery(id+"F16.imprint","IMPRINT",FACE,{"disambiguationData":[TD([[makeQuery(id+"F16.imprint","IMPRINT",EDGE,{"derivedFrom":sQuery(id+"F16.wireOp",EDGE,"E80")}),-1.0]])]});
            var Q2;
            Q2=makeQuery(id+"F16.imprint","IMPRINT",FACE,{"disambiguationData":[TD([[makeQuery(id+"F16.imprint","IMPRINT",EDGE,{"derivedFrom":sQuery(id+"F16.wireOp",EDGE,"E87.MirrorC")}),1.0]])]});
            var Q3;
            Q3=makeQuery(id+"F2.opExtrude","CAP_FACE",FACE,{"disambiguationData":[OSD([sQuery(id+"F0.wireOp",EDGE,"E12"),sQuery(id+"F0.wireOp",EDGE,"E13"),sQuery(id+"F0.wireOp",EDGE,"E14"),sQuery(id+"F0.wireOp",EDGE,"E15"),sQuery(id+"F0.wireOp",EDGE,"E17.filletArc"),sQuery(id+"F0.wireOp",EDGE,"E18.filletArc"),sQuery(id+"F0.wireOp",EDGE,"E19.filletArc"),sQuery(id+"F0.wireOp",EDGE,"E20.filletArc"),sQuery(id+"F0.wireOp",EDGE,"E25.0"),sQuery(id+"F0.wireOp",EDGE,"E25.1"),sQuery(id+"F0.wireOp",EDGE,"E25.2"),sQuery(id+"F0.wireOp",EDGE,"E25.3"),sQuery(id+"F0.wireOp",EDGE,"E25.4"),sQuery(id+"F0.wireOp",EDGE,"E25.5"),sQuery(id+"F0.wireOp",EDGE,"E25.6"),sQuery(id+"F0.wireOp",EDGE,"E25.7")])],"isStart":false});
            extrude(context, id + "F17", {"entities" : qUnion([Q0, Q1, Q2]), "endBound" : BoundingType.UP_TO_SURFACE, "endBoundEntityFace" : qUnion([Q3]), "depth" : 25 * mm});
        }
    });
